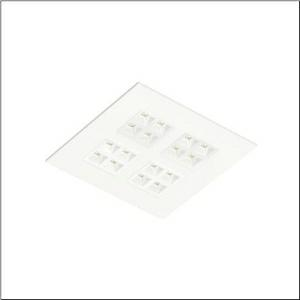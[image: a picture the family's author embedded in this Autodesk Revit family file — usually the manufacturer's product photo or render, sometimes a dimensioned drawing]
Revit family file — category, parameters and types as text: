
# Revit family: silica_r__31_square_51my6nds44wa_cdf9
name_source: partatom
category: Lighting Fixtures
units: mm (PartAtom-declared; Revit-internal decimal feet)

## family parameters
Cut with Voids When Loaded = No
Host = Face
Light Source = No
Part Type = Normal
Room Calculation Point = No
Round Connector Dimension = Use Diameter
Shared = No

## types (1)
- --- (1 x LED, 6640 lm, 38.5 W, 4000K)
    Apparent Load = 39 VA
    CIE Flux Codes = 81 99 100 100 100
    Color Rendering = 80
    Color Temperature = 4000K
    Default Elevation = 1800 mm
    Description = Silica® 31 Square, office luminaire, primary light control with lens, of PMMA, primary anti-glare with reflector, of PC, white, light emission: direct distribution, primary light characteristic: symmetric, installation type: lay-in mounting, LED, rated luminous flux: 4.570lm, luminous efficacy: 176lm/W, light colour: 840, colour temperature: 4000K, control gear: DALI 2, Multilumen, with terminal, 5-pole, mains connection: 220..240V, AC, 50/60Hz, rated input power: 26W, luminaire housing, of sheet steel, coated, traffic white (RAL 9016), module: M600, length: 595mm, width: 595mm, height: 43mm, protection rating (complete): IP20, insulation class (complete): insulation class II (safety insulation), certification: CE, impact resistance: IK03, permissible operating ambient temperature: -20..+35°C, standard: EN 50419, packaging unit: 1 piece
    Height = 0 mm  [stored 0 ft]
    Lamp = 1 x LED
    Lamp Light Flux = 6640 lm
    Lamp Power = 38.5 W
    Lamp count = 1
    Length = 595 mm
    Luminous efficacy = 172 lm/W
    Manufacturer = Siteco
    ModVariant = No
    Model = 51MY6NDS44WA
    Mounting Place = Ceiling
    Mounting Type = Recessed
    Number of Poles = 1
    OnlyDefault = Yes
    Power Factor = 1
    Product Name = Silica® 31 Square
    Product group = office luminaire | ceiling recessed
    ProductGroupID = 401
    Protection Class = Protection class II
    Protection Degree = IP 20
    RLX_Detail_Level = 1
    RLX_Emergency_Light_Flux = 0 lm
    RLX_Emergency_Type = 0
    RLX_Emergency_Type_DB = No
    RlxData = <blob elided: 28181 chars, md5=154655e7>
    Socket = socket
    Standby Power = 0 W
    System Light Flux = 6640 lm
    System Power = 39 W
    Type Comments = factory setting: luminous flux: 100 % | (OFF | OFF | OFF | OFF) | 1050 mA
    Type Image = l_1313651.jpg
    URL = http://relux.com
    VarID = @adj_036000
    Voltage = 0 V
    Weight = 0.00 kg
    Width = 595 mm

note: [stored X ft] marks values corroborated as IEEE doubles in the binary element streams (Revit-internal decimal feet)

## geometry (parser evidence)
native form markers: Blend x4, Sweep x12
no freeform markers — native parametric forms only
